# Revit family: Toilet-Floor_Mount-Elongated-American_Standard-Studio-2794.709
name_source: partatom
category: Plumbing Fixtures
units: mm (PartAtom-declared; Revit-internal decimal feet)

## family parameters
Always vertical = No
Cut with Voids When Loaded = No
OmniClass Number = 23.45.05.21.11.11
OmniClass Title = Water Operated Water Closets
Part Type = Normal
Room Calculation Point = No
Round Connector Dimension = Use Radius
Shared = Yes
Work Plane-Based = Yes

## types (1)
- 2794709.020
    ADA Compliant = Yes
    ASME A112.18.1/CSA B125.1 = Yes
    Assembly Code = D2010110
    Bowl Shape = Elongated
    CW Connection = Yes
    CWFU = 10
    Cold Water Connection Diameter = 3/8"
    Cold Water Connection Radius = 3/16"
    Cold Water Inlet = 8"
    Cold water parameter = 8"
    Default Elevation = 0"
    Description = Concealed Trapway Right Studio®Touchless Chair Height Elongated Toilet with Seat
    Finish = Vitreous China-American Standard-020-White
    Flush Rate = 1.28 gpf/4.8 Lpf
    HW Connection = No
    HWFU = 0
    Height = 30 11/16"
    Inlet 2.25" = No
    Inlet 8" = Yes
    Installation Type = Floor Mounted
    Length = 30 3/16"
    Manufacturer = American Standard
    Material = Vitreous China-American Standard-020-White
    Model = 2794709
    Price = Prices may vary. Please consult Manufacturer Representative for most up-to-date price list.
    Product Documentation Link = https://www.americanstandard.ca
    Product Page URL = https://www.americanstandard.ca
    Revised Date = 09/13/2021
    Sensor Height Optional = 36"
    Sensor Top of the Tank = Yes
    Sensor Wall Mount = No
    URL = http://www.americanstandard.ca
    Vent Connection = No
    WFU = 10
    Warranty Information = Lifetime warranty on chinaware, 5 year warranty on all mechanical parts, and 1 year warranty on seat
    Waste Connection = Yes
    Waste Connection Diameter = 2 1/8"
    Waste Connection Radius = 1 1/16"
    Width = 15 13/16"

## geometry (parser evidence)
native form markers: Sweep x2
no freeform markers — native parametric forms only
